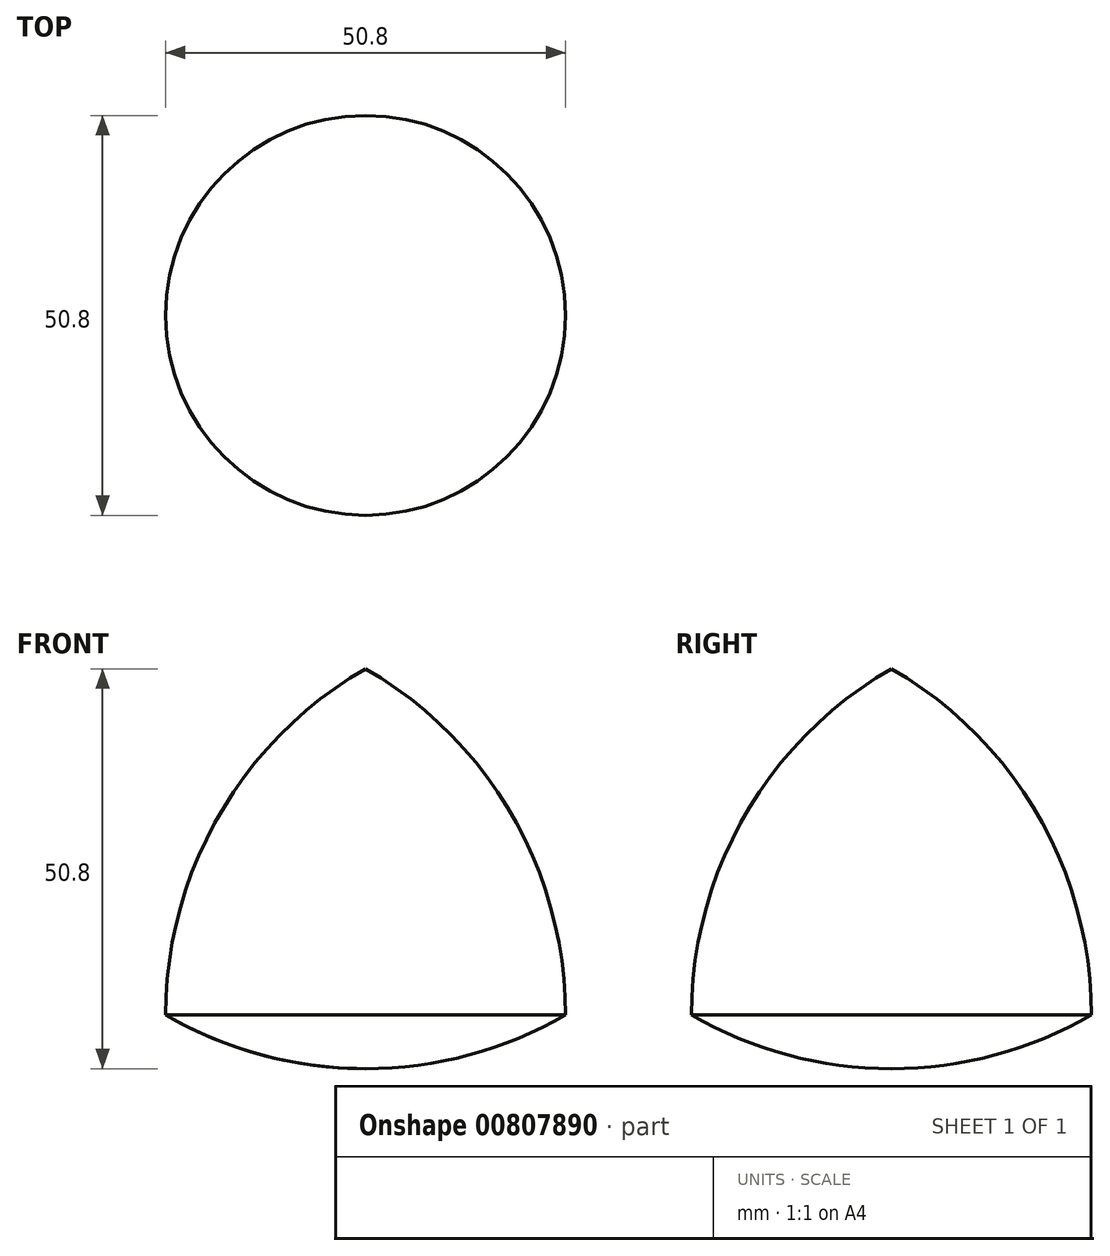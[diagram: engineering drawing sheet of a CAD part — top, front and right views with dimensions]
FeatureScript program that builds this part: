
annotation { "Feature Type Name" : "Feature", "Feature Type Description" : "" }
export const myFeature = defineFeature(function(context is Context, id is Id, definition is map)
    precondition{}
    {
        {
            var Q0;
            Q0=qCreatedBy(makeId("Front.planeOp"),FACE);
            var sketch = newSketch(context, id + "F0", { "sketchPlane" : qUnion([Q0])});
            skLineSegment(sketch, "E0", {"start": v(-4.56, 53.9) * mm, "end": v(-29.96, 9.91) * mm});
            skLineSegment(sketch, "E1", {"start": v(-29.96, 9.91) * mm, "end": v(20.84, 9.91) * mm});
            skLineSegment(sketch, "E2", {"start": v(20.84, 9.91) * mm, "end": v(-4.56, 53.9) * mm});
            skArc(sketch, "E3", {"start": v(-4.56, 53.9) * mm, "mid": v(-23.15, 35.31) * mm, "end": v(-29.96, 9.91) * mm});
            skArc(sketch, "E4", {"start": v(20.84, 9.91) * mm, "mid": v(14.03, 35.31) * mm, "end": v(-4.56, 53.9) * mm});
            skArc(sketch, "E5", {"start": v(-29.96, 9.91) * mm, "mid": v(-4.56, 3.1) * mm, "end": v(20.84, 9.91) * mm});
            skLineSegment(sketch, "E6", {"start": v(-4.56, 53.9) * mm, "end": v(-4.56, 9.91) * mm});
            skLineSegment(sketch, "E7", {"start": v(-4.56, 9.91) * mm, "end": v(-4.56, 3.1) * mm});
            skSolve(sketch);
        }
        {
            var Q0;
            Q0=makeQuery(id+"F0.imprint","IMPRINT",FACE,{"disambiguationData":[TD([[makeQuery(id+"F0.imprint","IMPRINT",EDGE,{"derivedFrom":sQuery(id+"F0.wireOp",EDGE,"E0")}),-1.0]])]});
            var Q1;
            {var subQ0=sQuery(id+"F0.wireOp",EDGE,"E0");Q1=makeQuery(id+"F0.imprint","IMPRINT",FACE,{"disambiguationData":[TD([[makeQuery(id+"F0.imprint","IMPRINT",EDGE,{"derivedFrom":subQ0}),1.0]])]});}
            var Q2;
            {var subQ3=sQuery(id+"F0.wireOp",EDGE,"E7");Q2=makeQuery(id+"F0.imprint","IMPRINT",FACE,{"disambiguationData":[TD([[makeQuery(id+"F0.imprint","IMPRINT",EDGE,{"derivedFrom":subQ3}),-1.0]])]});}
            var Q3;
            Q3=sQuery(id+"F0.wireOp",EDGE,"E6");
            revolve(context, id + "F1", {"surfaceOperationType" : NewSurfaceOperationType.NEW, "entities" : qUnion([Q0, Q1, Q2]), "axis" : qUnion([Q3]), "revolveType" : RevolveType.FULL});
        }
    });
